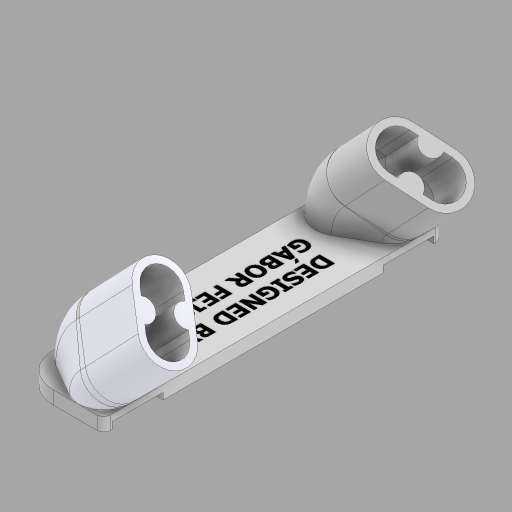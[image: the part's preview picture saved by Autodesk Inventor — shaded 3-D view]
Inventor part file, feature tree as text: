
AUTODESK INVENTOR PART (.ipt)
format: ipt  version: 2023 (Build 270158000, 158)  size: 1,152,000 bytes
history: native  units: mm
features: extrude x17, sketch x12, plane x2, revolve x2, chamfer x2, fillet x2, sweep x1, mirror x1
ambient origin geometry x8: Origin, YZ Plane, XZ Plane, XY Plane, X Axis, Y Axis, Z Axis, Center Point
bodies: Solid1 (feature_tree)
feature tree (39):
  sketch  "Sketch1"  dims[d0=100.0mm d1=25.0mm d2=7.5mm d3=7.5mm d4=60.0deg d5=15.0mm d6=11.0mm d7=11.0mm d8=15.0mm d11=135.0deg]
  plane  "Work Plane1"
  sweep  "Sweep1"
  extrude  "Extrusion1"  Depth=4.0mm TaperAngle=0.0deg
  revolve  "Revolution1"  Angle=45.0deg
  sketch  "Sketch6"  dims[d31=10.0mm d32=45.0deg]
  extrude  "Extrusion4"  TaperAngle=45.0deg  [1 undecoded]
  extrude  "Extrusion5"  Depth=10.0mm
  sketch  "Sketch7"  dims[d33=10.0mm d34=10.0mm]
  extrude  "Extrusion6"  Depth=10.0mm
  extrude  "Extrusion7"  Depth=15.0mm
  mirror  "Mirror4"
  plane  "Work Plane9"
  extrude  "Extrusion8"  Depth=5.5mm
  revolve  "Revolution2"  [1 undecoded]
  extrude  "Extrusion9"  Depth=6.5mm
  sketch  "Sketch19"  dims[d60=5.5mm d61=5.5mm]
  extrude  "Extrusion10"  Depth=20.0mm TaperAngle=0.0deg
  extrude  "Extrusion11"  Depth=10.0mm
  extrude  "Extrusion12"  TaperAngle=90.0deg  [1 undecoded]
  sketch  "Sketch21"  dims[d65=2.0mm d66=6.5mm]
  extrude  "Extrusion13"  Depth=10.0mm
  chamfer  "Chamfer3"  Distance=5.5mm
  extrude  "Extrusion15"  Depth=10.0mm
  extrude  "Extrusion18"  Depth=10.0mm
  fillet  "Fillet2"  Radius=11.0mm
  fillet  "Fillet3"  Radius=11.0mm
  extrude  "Extrusion19"  Depth=10.0mm
  extrude  "Extrusion20"  Depth=10.0mm
  extrude  "Extrusion21"  Depth=10.0mm
  extrude  "Extrusion22"  Depth=10.0mm TaperAngle=0.0deg
  chamfer  "Chamfer5"  Distance=10.0mm
  sketch  "Sketch3"  dims[d12=0.0mm d13=0.0mm d14=4.0mm d15=0.0mm]
  sketch  "Sketch5"  dims[d29=11.389087mm d30=45.0deg]
  sketch  "Sketch14"  dims[d35=45.0deg d37=10.0mm]
  sketch  "Sketch15"  dims[d38=0.977384mm d57=15.0mm]
  sketch  "Sketch20"  dims[d63=11.0mm d64=11.0mm]
  sketch  "Sketch22"  dims[d67=6.5mm d68=20.0mm d69=0.0mm]
  sketch  "Sketch23"  dims[d70=325.0mm d71=0.0mm d72=7.5mm d73=90.0deg d74=7.5mm d75=5.5mm d76=5.5mm d77=15.0mm d78=11.0mm d79=11.0mm d80=2.0mm d81=6.5mm d82=6.5mm d83=10.0mm d84=0.0mm d93=10.0mm d94=0.0mm d115=20.0mm d116=0.0mm d131=8.726646mm d132=300.0mm d133=0.0mm d134=15.0mm d135=300.0mm d136=0.0mm d137=11.0mm d138=11.0mm d139=2.0mm d140=6.5mm d141=6.5mm d142=10.0mm d143=0.0mm d144=40.0mm d145=0.0mm d146=25.0mm d147=100.0mm d150=15.0mm d151=5.5mm d152=2.0mm d153=0.0mm d156=2.0mm d157=4.0mm d158=45.0deg d162=549.891mm d163=50.0mm d164=100.0mm d167=2.5mm d169=15.0mm d170=17.5mm d171=17.5mm d174=10.0mm d175=300.0mm d176=0.0mm d177=7.5mm d183=2.0mm d184=0.0mm d185=2.0mm d186=10.0mm d187=3.0mm d188=0.0mm d189=15.0mm d190=0.0mm d191=1.0mm d192=0.0mm d193=6.5mm d194=10.0mm d195=0.0mm d196=2.0mm d197=4.0mm d198=45.0deg d178=0.872665mm]
note: 3 required parameter values undecoded (feature->parameter linkage not recoverable at this tier; creation-order binding heuristic only, values carry confidence <= 0.55)